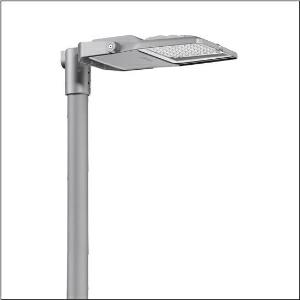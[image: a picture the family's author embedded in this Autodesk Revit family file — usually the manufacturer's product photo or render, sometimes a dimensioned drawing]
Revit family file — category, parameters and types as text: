
# Revit family: floodlight_fl_21_iq_mini___pl52_5xa7771d2d3a_64cb
name_source: partatom
category: Lighting Fixtures
units: mm (PartAtom-declared; Revit-internal decimal feet)

## family parameters
Cut with Voids When Loaded = No
Host = Face
Light Source = No
Part Type = Normal
Room Calculation Point = No
Round Connector Dimension = Use Diameter
Shared = No

## types (1)
- --- (1 x LED, 17830 lm, 143 W, 3000K)
    Apparent Load = 143 VA
    CIE Flux Codes = 26 60 98 100 100
    Color Rendering = 70
    Color Temperature = 3000K
    Default Elevation = 1800 mm
    Description = Floodlight FL 21 iQ mini, floodlight, primary light control with lens, of PMMA, primary optical cover: protective disc, of toughened safety glass, transparent, light distribution: PL52, light emission: direct distribution, installation type: surface-mounted, LED, High Power LED, rated luminous flux: 17.830lm, luminous efficacy: 125lm/W, light colour: 730, colour temperature: 3000K, control: Auto-Match, Temp-Guard, Lumen-Switch, Night-Set, Smart-Wire, Light-Fading, Desk-Remote (wireless, voltage-free reading and setting of iQ features in the workshop via application-optimized NFC function/RFID function), optimised constant luminous flux control (CLO 2.0), with terminal, 6-pole, mains connection: 220..240V, AC, 50/60Hz, start of lifetime: 143W, end of service life: 152W, reduction: 61W, luminaire housing, of diecast aluminium, powder-coated, Siteco® metallic grey (DB 702S), corrosivity category C5 mid according to DIN EN ISO 12944, sealing non-destructively replaceable, please order mast flange separately, mast bracket, of steel, galvanised, powder-coated, Siteco® metallic grey (DB 702S), protection rating (complete): IP66, insulation class (complete): insulation class II (safety insulation), certification: CE, ENEC, VDE, protection symbol: D, impact resistance: IK08, permissible operating ambient temperature: -40..+40°C, permissible operating ambient temperature for outdoor applications: -40..+50°C, standard: DIN EN 12944, LABS conformity tested according to VDMA 24364:2018-05, packaging unit: 1 piece

Light Distribution: PL52
    Height = 70 mm
    Lamp = 1 x LED
    Lamp Light Flux = 17830 lm
    Lamp Power = 143 W
    Lamp count = 1
    Length = 485 mm
    Luminous efficacy = 125 lm/W
    Manufacturer = Siteco
    ModVariant = No
    Model = 5XA7771D2D3A
    Number of Poles = 1
    OnlyDefault = Yes
    Power Factor = 1
    Product Name = Floodlight FL 21 iQ mini | PL52
    Product group = floodlight | pylon annexe
    ProductGroupID = 6200
    Protection Class = Protection class II
    Protection Degree = IP 66
    RLX_Detail_Level = 1
    RLX_Emergency_Light_Flux = 0 lm
    RLX_Emergency_Type = 0
    RLX_Emergency_Type_DB = No
    RlxData = <blob elided: 101781 chars, md5=9e5b2ca0>
    Socket = socket
    Standby Power = 0 W
    System Light Flux = 17830 lm
    System Power = 143 W
    Type Comments = factory setting: luminous flux: 100 % | dim-lin: 254 | 730 mA
    Type Image = l_1007125.jpg
    URL = http://relux.com
    VarID = @adj_096277
    Voltage = 0 V
    Weight = 0.00 kg
    Width = 337 mm

## geometry (parser evidence)
native form markers: Blend x4, Sweep x13
no freeform markers — native parametric forms only
